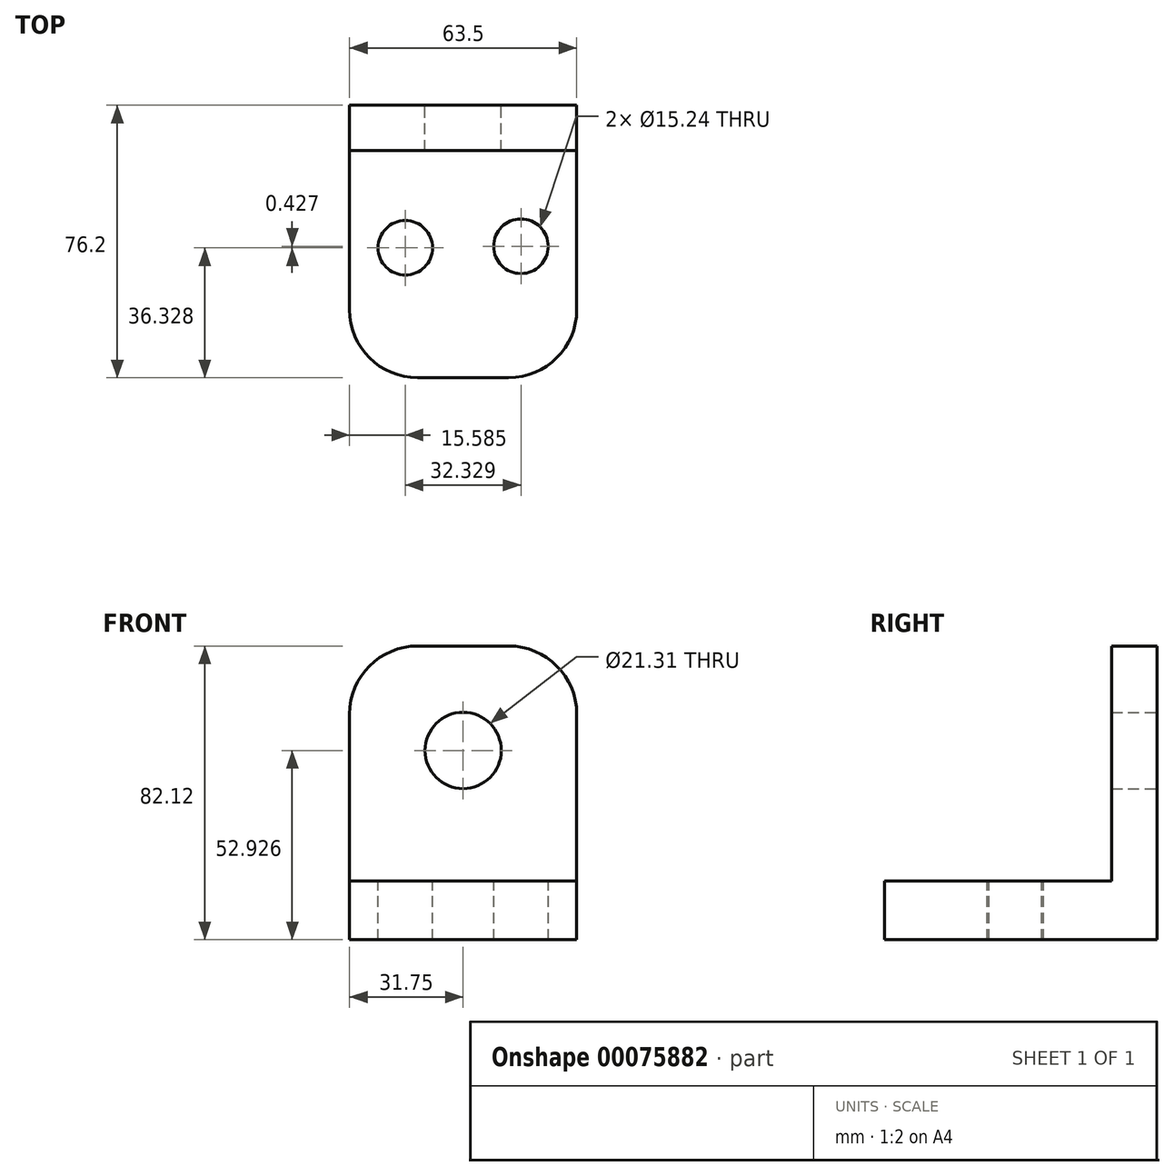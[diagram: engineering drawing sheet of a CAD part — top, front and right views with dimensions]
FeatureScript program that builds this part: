
annotation { "Feature Type Name" : "Feature", "Feature Type Description" : "" }
export const myFeature = defineFeature(function(context is Context, id is Id, definition is map)
    precondition{}
    {
        {
            var Q0;
            Q0=qCreatedBy(makeId("Front.planeOp"),FACE);
            var sketch = newSketch(context, id + "F0", { "sketchPlane" : qUnion([Q0])});
            skLineSegment(sketch, "E0.bottom", {"start": v(31.75, 8.12) * mm, "end": v(-31.75, 8.12) * mm});
            skLineSegment(sketch, "E0.top", {"start": v(31.75, -8.12) * mm, "end": v(-31.75, -8.12) * mm});
            skLineSegment(sketch, "E0.left", {"start": v(31.75, 8.12) * mm, "end": v(31.75, -8.12) * mm});
            skLineSegment(sketch, "E0.right", {"start": v(-31.75, 8.12) * mm, "end": v(-31.75, -8.12) * mm});
            skPoint(sketch, "E0.middle", {"position": v(0, 0) * mm});
            skLineSegment(sketch, "E1.bottom", {"start": v(-31.75, 8.12) * mm, "end": v(31.75, 8.12) * mm});
            skLineSegment(sketch, "E1.top", {"start": v(-12.7, 74) * mm, "end": v(12.7, 74) * mm});
            skLineSegment(sketch, "E1.left", {"start": v(-31.75, 8.12) * mm, "end": v(-31.75, 54.95) * mm});
            skLineSegment(sketch, "E1.right", {"start": v(31.75, 8.12) * mm, "end": v(31.75, 54.95) * mm});
            skPoint(sketch, "E2.visualSharp", {"position": v(-31.75, 74) * mm});
            skArc(sketch, "E2.filletArc", {"start": v(-12.7, 74) * mm, "mid": v(-26.17, 68.42) * mm, "end": v(-31.75, 54.95) * mm});
            skPoint(sketch, "E3.visualSharp", {"position": v(31.75, 74) * mm});
            skArc(sketch, "E3.filletArc", {"start": v(31.75, 54.95) * mm, "mid": v(26.17, 68.42) * mm, "end": v(12.7, 74) * mm});
            skSolve(sketch);
        }
        {
            var Q0;
            Q0=qCreatedBy(makeId("Front.planeOp"),FACE);
            var sketch = newSketch(context, id + "F1", { "sketchPlane" : qUnion([Q0])});
            skCircle(sketch, "E4", {"center": v(0, 44.8) * mm, "radius": 10.65 * mm});
            skSolve(sketch);
        }
        {
            var Q0;
            Q0 = qSketchRegion(id + "F0", true);
            extrude(context, id + "F2", {"entities" : qUnion([Q0]), "depth" : 12.7 * mm});
        }
        {
            var Q0;
            Q0 = qSketchRegion(id + "F1", true);
            extrude(context, id + "F3", {"entities" : qUnion([Q0]), "operationType" : NewBodyOperationType.REMOVE, "depth" : 12.7 * mm});
        }
        {
            var Q0;
            Q0=makeQuery(id+"F2.opExtrude","CAP_FACE",FACE,{"disambiguationData":[OSD([sQuery(id+"F0.wireOp",EDGE,"E0.top"),sQuery(id+"F0.wireOp",EDGE,"E0.left"),sQuery(id+"F0.wireOp",EDGE,"E0.right"),sQuery(id+"F0.wireOp",EDGE,"E1.top"),sQuery(id+"F0.wireOp",EDGE,"E1.left"),sQuery(id+"F0.wireOp",EDGE,"E1.right"),sQuery(id+"F0.wireOp",EDGE,"E2.filletArc"),sQuery(id+"F0.wireOp",EDGE,"E3.filletArc")])],"isStart":false});
            var sketch = newSketch(context, id + "F4", { "sketchPlane" : qUnion([Q0])});
            skLineSegment(sketch, "E5.bottom", {"start": v(-31.75, -8.12) * mm, "end": v(31.75, -8.12) * mm});
            skLineSegment(sketch, "E5.top", {"start": v(-31.75, 8.33) * mm, "end": v(31.75, 8.33) * mm});
            skLineSegment(sketch, "E5.left", {"start": v(-31.75, -8.12) * mm, "end": v(-31.75, 8.33) * mm});
            skLineSegment(sketch, "E5.right", {"start": v(31.75, -8.12) * mm, "end": v(31.75, 8.33) * mm});
            skSolve(sketch);
        }
        {
            var Q0;
            Q0 = qSketchRegion(id + "F4", true);
            extrude(context, id + "F5", {"entities" : qUnion([Q0]), "operationType" : NewBodyOperationType.ADD, "depth" : 63.5 * mm});
        }
        {
            var Q0;
            Q0=makeQuery(id+"F5.opExtrude","CAP_EDGE",EDGE,{"disambiguationData":[OSD([sQuery(id+"F4.wireOp",EDGE,"E5.left")])],"isStart":false});
            fillet(context, id + "F6", {"entities" : qUnion([Q0]), "radius" : 19.05 * mm, "tangentPropagation" : true, "allowEdgeOverflow" : false});
        }
        {
            var Q0;
            Q0=makeQuery(id+"F5.opExtrude","CAP_EDGE",EDGE,{"disambiguationData":[OSD([sQuery(id+"F4.wireOp",EDGE,"E5.right")])],"isStart":false});
            fillet(context, id + "F7", {"entities" : qUnion([Q0]), "radius" : 19.05 * mm, "tangentPropagation" : true, "allowEdgeOverflow" : false});
        }
        {
            var Q0;
            Q0=qCreatedBy(makeId("Top.planeOp"),FACE);
            var sketch = newSketch(context, id + "F8", { "sketchPlane" : qUnion([Q0])});
            skCircle(sketch, "E6", {"center": v(-16.17, -39.87) * mm, "radius": 7.62 * mm});
            skCircle(sketch, "E7", {"center": v(16.16, -39.45) * mm, "radius": 7.62 * mm});
            skSolve(sketch);
        }
        {
            var Q0;
            Q0 = qSketchRegion(id + "F8", true);
            extrude(context, id + "F9", {"entities" : qUnion([Q0]), "operationType" : NewBodyOperationType.REMOVE, "endBound" : BoundingType.SYMMETRIC, "oppositeDirection" : true, "depth" : 50.8 * mm});
        }
    });
